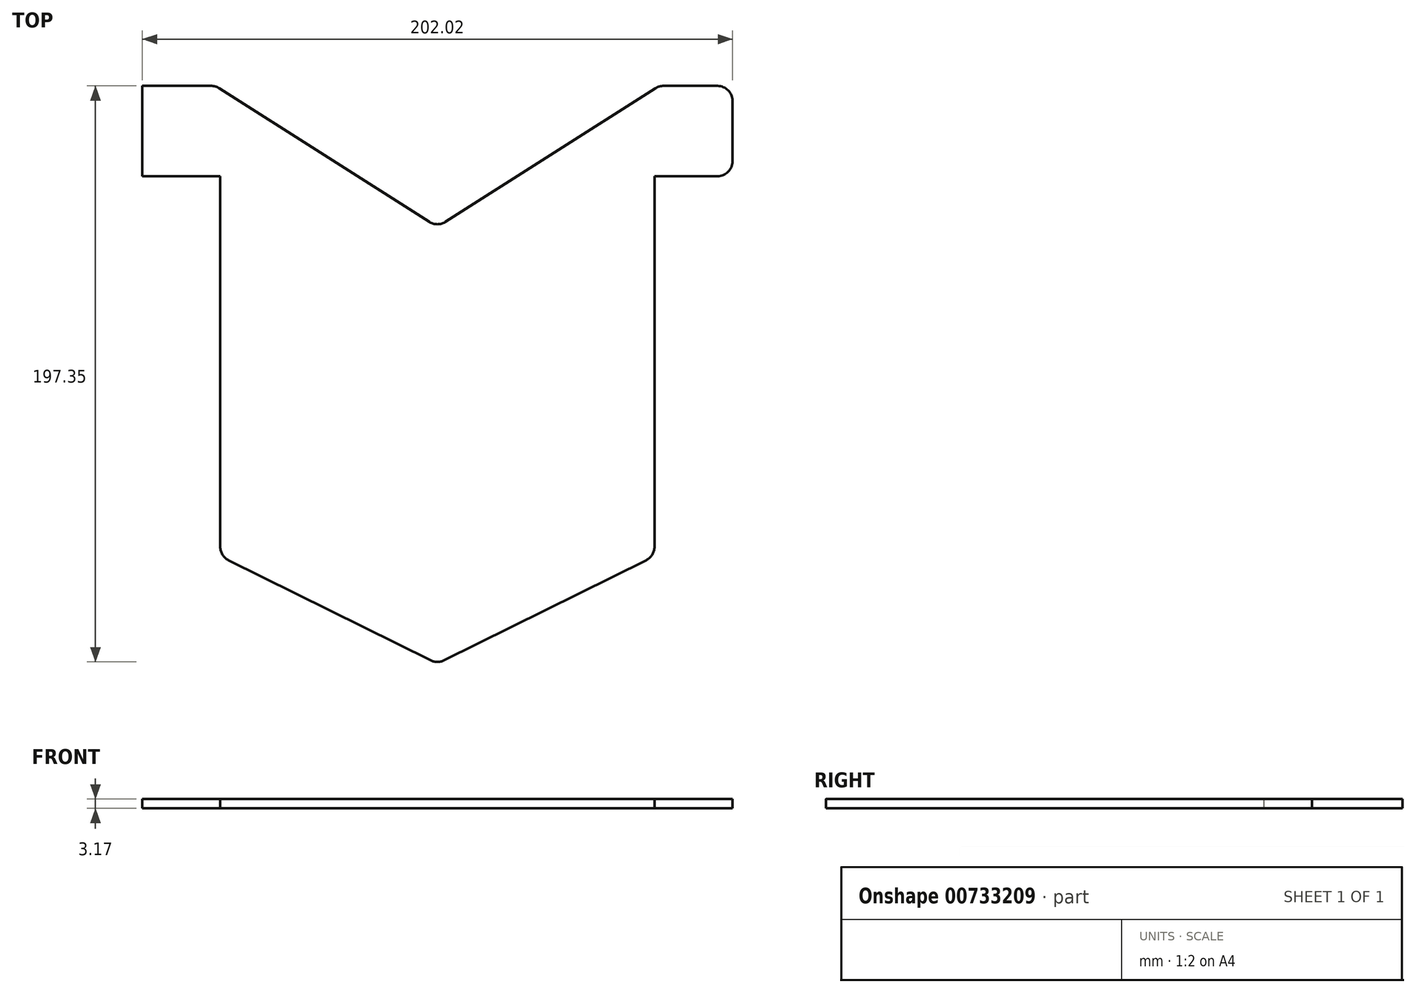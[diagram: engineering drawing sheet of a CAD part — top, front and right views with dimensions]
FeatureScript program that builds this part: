
annotation { "Feature Type Name" : "Feature", "Feature Type Description" : "" }
export const myFeature = defineFeature(function(context is Context, id is Id, definition is map)
    precondition{}
    {
        {
            var Q0;
            Q0=qCreatedBy(makeId("Top.planeOp"),FACE);
            var sketch = newSketch(context, id + "F0", { "sketchPlane" : qUnion([Q0])});
            skPoint(sketch, "E0", {"position": v(-53.73, 0) * mm});
            skLineSegment(sketch, "E1", {"start": v(-53.73, 0) * mm, "end": v(0, -34.22) * mm});
            skLineSegment(sketch, "E2", {"start": v(-101.01, 7.57) * mm, "end": v(-101.01, -43.23) * mm});
            skLineSegment(sketch, "E3", {"start": v(-101.01, -43.23) * mm, "end": v(-74.34, -43.23) * mm});
            skLineSegment(sketch, "E4", {"start": v(-74.34, -43.23) * mm, "end": v(-74.34, -119.43) * mm});
            skLineSegment(sketch, "E5.top", {"start": v(-53.73, 33.15) * mm, "end": v(-101.01, 33.15) * mm});
            skLineSegment(sketch, "E5.left", {"start": v(-53.73, 0) * mm, "end": v(-53.73, 33.15) * mm});
            skLineSegment(sketch, "E5.right", {"start": v(-101.01, 0) * mm, "end": v(-101.01, 33.15) * mm});
            skLineSegment(sketch, "E6", {"start": v(-74.34, -119.43) * mm, "end": v(-74.34, -146.94) * mm});
            skLineSegment(sketch, "E7", {"start": v(-74.34, -146.94) * mm, "end": v(0, -183.82) * mm});
            skLineSegment(sketch, "E8", {"start": v(-101.01, 33.15) * mm, "end": v(-101.01, -43.23) * mm});
            skLineSegment(sketch, "E9", {"start": v(0, 77.83) * mm, "end": v(0, -209.59) * mm});
            skLineSegment(sketch, "E10.MirrorCS", {"start": v(53.73, 0) * mm, "end": v(0, -34.22) * mm});
            skLineSegment(sketch, "E11.MirrorCS", {"start": v(53.73, 0) * mm, "end": v(53.73, 33.15) * mm});
            skLineSegment(sketch, "E12.MirrorCS", {"start": v(53.73, 33.15) * mm, "end": v(101.01, 33.15) * mm});
            skLineSegment(sketch, "E13.MirrorCS", {"start": v(101.01, 33.15) * mm, "end": v(101.01, -43.23) * mm});
            skLineSegment(sketch, "E14.MirrorCS", {"start": v(101.01, -43.23) * mm, "end": v(74.34, -43.23) * mm});
            skLineSegment(sketch, "E15.MirrorCS", {"start": v(74.34, -43.23) * mm, "end": v(74.34, -119.43) * mm});
            skLineSegment(sketch, "E16.MirrorCS", {"start": v(74.34, -119.43) * mm, "end": v(74.34, -146.94) * mm});
            skLineSegment(sketch, "E17.MirrorCS", {"start": v(74.34, -146.94) * mm, "end": v(0, -183.82) * mm});
            skLineSegment(sketch, "E18", {"start": v(0, -34.22) * mm, "end": v(-75.9, 14.12) * mm});
            skLineSegment(sketch, "E19", {"start": v(-75.9, 14.12) * mm, "end": v(-101.01, 14.12) * mm});
            skLineSegment(sketch, "E20.MirrorCS", {"start": v(0, -34.22) * mm, "end": v(75.9, 14.12) * mm});
            skLineSegment(sketch, "E21.MirrorCS", {"start": v(75.9, 14.12) * mm, "end": v(101.01, 14.12) * mm});
            skLineSegment(sketch, "E22", {"start": v(-74.34, -43.23) * mm, "end": v(-74.34, -16.81) * mm});
            skLineSegment(sketch, "E23", {"start": v(-74.34, -16.81) * mm, "end": v(-101.01, -16.81) * mm});
            skLineSegment(sketch, "E24.MirrorCS", {"start": v(74.34, -43.23) * mm, "end": v(74.34, -16.81) * mm});
            skLineSegment(sketch, "E25.MirrorCS", {"start": v(74.34, -16.81) * mm, "end": v(101.01, -16.81) * mm});
            skSolve(sketch);
        }
        {
            var Q0;
            Q0=makeQuery(id+"F0.imprint","IMPRINT",FACE,{"disambiguationData":[TD([[makeQuery(id+"F0.imprint","IMPRINT",EDGE,{"derivedFrom":sQuery(id+"F0.wireOp",EDGE,"E4")}),1.0]])]});
            var Q1;
            Q1=makeQuery(id+"F0.imprint","IMPRINT",FACE,{"disambiguationData":[TD([[makeQuery(id+"F0.imprint","IMPRINT",EDGE,{"derivedFrom":sQuery(id+"F0.wireOp",EDGE,"E15.MirrorCS")}),-1.0]])]});
            extrude(context, id + "F1", {"entities" : qUnion([Q0, Q1]), "depth" : 3.17 * mm, "offsetDistance" : 25.4 * mm});
        }
        {
            var Q0;
            Q0=makeQuery(id+"F1.opExtrude","SWEPT_EDGE",EDGE,{"disambiguationData":[OSD([sQuery(id+"F0.wireOp",EDGE,"E1"),sQuery(id+"F0.wireOp",EDGE,"UrVhNKhP-I4kY-EzzC-LhI9-ELALRTyGq8Mb")])]});
            var Q1;
            Q1=makeQuery(id+"F1.opExtrude","SWEPT_EDGE",EDGE,{"disambiguationData":[OSD([sQuery(id+"F0.wireOp",EDGE,"E10.MirrorCS"),sQuery(id+"F0.wireOp",EDGE,"E11.MirrorCS")])]});
            var Q2;
            Q2=makeQuery(id+"F1.opExtrude","SWEPT_EDGE",EDGE,{"disambiguationData":[OSD([sQuery(id+"F0.wireOp",EDGE,"E1"),sQuery(id+"F0.wireOp",EDGE,"E9"),sQuery(id+"F0.wireOp",EDGE,"E10.MirrorCS")])]});
            fillet(context, id + "F2", {"entities" : qUnion([Q0, Q1, Q2]), "radius" : 5.08 * mm, "tangentPropagation" : true, "allowEdgeOverflow" : false});
        }
        {
            var Q0;
            Q0=makeQuery(id+"F1.opExtrude","SWEPT_EDGE",EDGE,{"disambiguationData":[OSD([sQuery(id+"F0.wireOp",EDGE,"E3"),sQuery(id+"F0.wireOp",EDGE,"E8")])]});
            var Q1;
            Q1=makeQuery(id+"F1.opExtrude","SWEPT_EDGE",EDGE,{"disambiguationData":[OSD([sQuery(id+"F0.wireOp",EDGE,"E6"),sQuery(id+"F0.wireOp",EDGE,"E7")])]});
            var Q2;
            Q2=makeQuery(id+"F1.opExtrude","SWEPT_EDGE",EDGE,{"disambiguationData":[OSD([sQuery(id+"F0.wireOp",EDGE,"E7"),sQuery(id+"F0.wireOp",EDGE,"E9"),sQuery(id+"F0.wireOp",EDGE,"E17.MirrorCS")])]});
            var Q3;
            Q3=makeQuery(id+"F1.opExtrude","SWEPT_EDGE",EDGE,{"disambiguationData":[OSD([sQuery(id+"F0.wireOp",EDGE,"E16.MirrorCS"),sQuery(id+"F0.wireOp",EDGE,"E17.MirrorCS")])]});
            var Q4;
            Q4=makeQuery(id+"F1.opExtrude","SWEPT_EDGE",EDGE,{"disambiguationData":[OSD([sQuery(id+"F0.wireOp",EDGE,"E13.MirrorCS"),sQuery(id+"F0.wireOp",EDGE,"E14.MirrorCS")])]});
            fillet(context, id + "F3", {"entities" : qUnion([Q0, Q1, Q2, Q3, Q4]), "radius" : 5.08 * mm, "tangentPropagation" : true, "allowEdgeOverflow" : false});
        }
        {
            var Q0;
            Q0=makeQuery(id+"F1.opExtrude","SWEPT_EDGE",EDGE,{"disambiguationData":[OSD([sQuery(id+"F0.wireOp",EDGE,"E18"),sQuery(id+"F0.wireOp",EDGE,"E19")])]});
            var Q1;
            Q1=makeQuery(id+"F1.opExtrude","SWEPT_EDGE",EDGE,{"disambiguationData":[OSD([sQuery(id+"F0.wireOp",EDGE,"E20.MirrorCS"),sQuery(id+"F0.wireOp",EDGE,"E21.MirrorCS")])]});
            fillet(context, id + "F4", {"entities" : qUnion([Q0, Q1]), "radius" : 5.08 * mm, "tangentPropagation" : true, "allowEdgeOverflow" : false});
        }
    });
